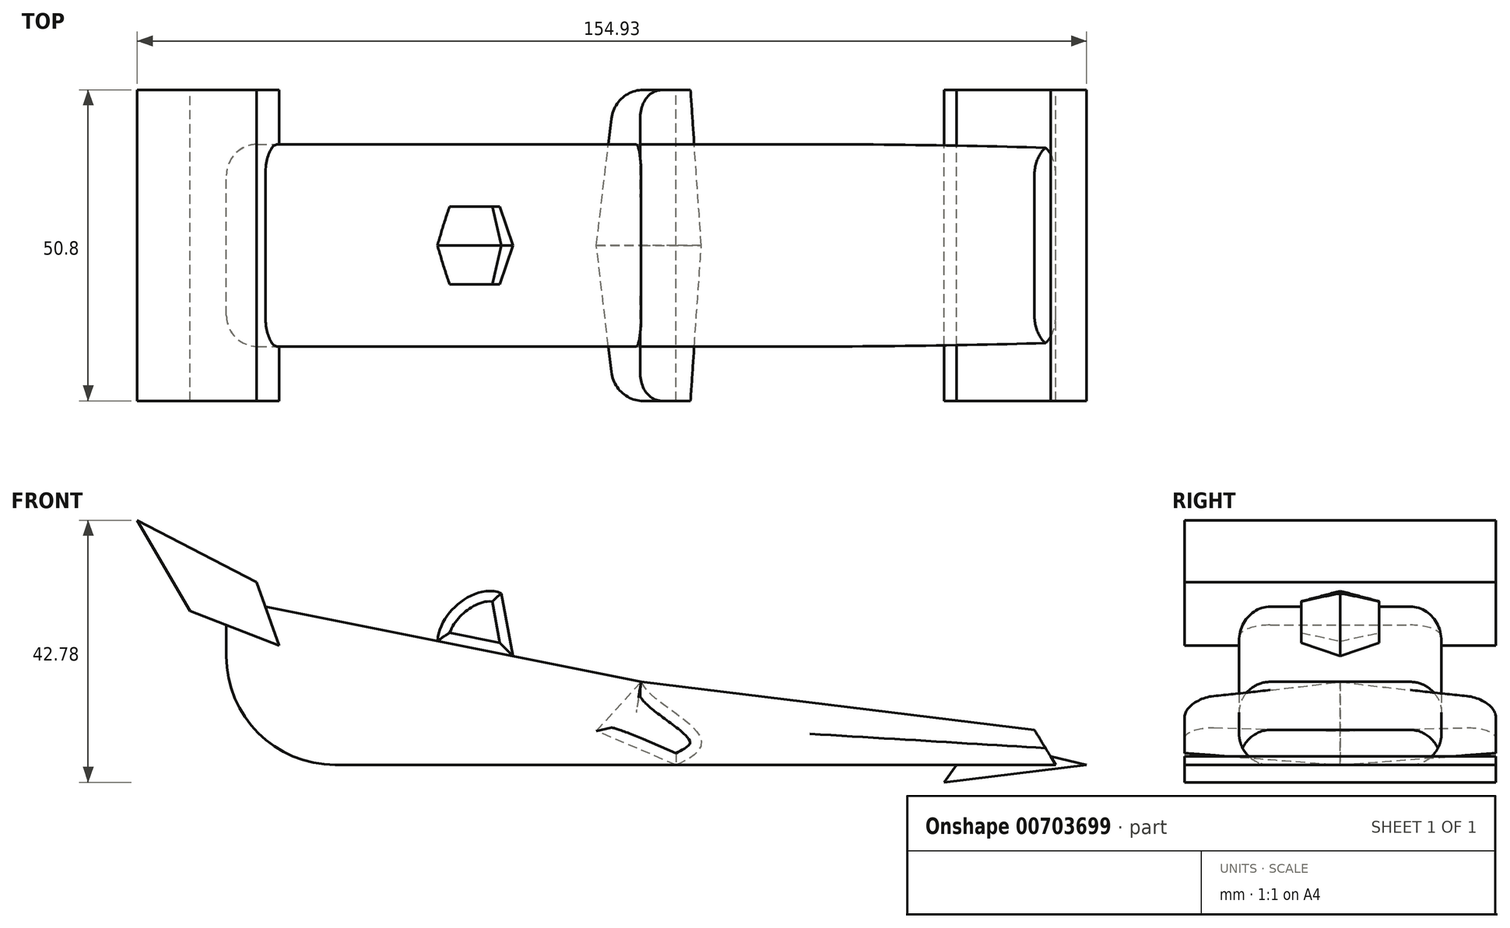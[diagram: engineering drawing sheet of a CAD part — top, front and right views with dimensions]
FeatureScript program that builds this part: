
annotation { "Feature Type Name" : "Feature", "Feature Type Description" : "" }
export const myFeature = defineFeature(function(context is Context, id is Id, definition is map)
    precondition{}
    {
        {
            var Q0;
            Q0=qCreatedBy(makeId("Front.planeOp"),FACE);
            var sketch = newSketch(context, id + "F0", { "sketchPlane" : qUnion([Q0])});
            skLineSegment(sketch, "E0.top", {"start": v(-49.9, -13.56) * mm, "end": v(67.68, -13.56) * mm});
            skLineSegment(sketch, "E0.left", {"start": v(-67.68, 13.56) * mm, "end": v(-67.68, 4.22) * mm});
            skPoint(sketch, "E0.middle", {"position": v(0, 0) * mm});
            skLineSegment(sketch, "E1", {"start": v(-67.68, 13.56) * mm, "end": v(67.68, -13.56) * mm});
            skLineSegment(sketch, "E2", {"start": v(-73.6, 11.59) * mm, "end": v(-59.05, 5.92) * mm});
            skLineSegment(sketch, "E3", {"start": v(-59.05, 5.92) * mm, "end": v(-62.75, 16.27) * mm});
            skLineSegment(sketch, "E4", {"start": v(-62.75, 16.27) * mm, "end": v(-82.23, 26.38) * mm});
            skLineSegment(sketch, "E5", {"start": v(-82.23, 26.38) * mm, "end": v(-73.6, 11.59) * mm});
            skPoint(sketch, "E6.visualSharp", {"position": v(-67.68, -13.56) * mm});
            skArc(sketch, "E6.filletArc", {"start": v(-67.68, 4.22) * mm, "mid": v(-62.47, -8.35) * mm, "end": v(-49.9, -13.56) * mm});
            skLineSegment(sketch, "E7", {"start": v(54.6, -9.2) * mm, "end": v(72.7, -13.56) * mm});
            skLineSegment(sketch, "E8", {"start": v(72.7, -13.56) * mm, "end": v(49.42, -16.4) * mm});
            skLineSegment(sketch, "E9", {"start": v(49.42, -16.4) * mm, "end": v(54.6, -9.2) * mm});
            skLineSegment(sketch, "E10", {"start": v(-20.58, 2.25) * mm, "end": v(-22.8, 14.44) * mm});
            skFitSpline(sketch, "E11", {"points": [v(-22.8, 14.44) * mm, v(-32.22, 3) * mm], "startDerivative": vector(-14.14, 6.72) * mm, "endDerivative": vector(11.97, -18.48) * mm});
            skLineSegment(sketch, "E12", {"start": v(-32.22, 3) * mm, "end": v(-20.58, 2.25) * mm});
            skLineSegment(sketch, "E13", {"start": v(0, 0) * mm, "end": v(64.19, -7.85) * mm});
            skLineSegment(sketch, "E14", {"start": v(64.19, -7.85) * mm, "end": v(67.68, -13.56) * mm});
            skCircle(sketch, "E15", {"center": v(-60.07, -7.54) * mm, "radius": 11.65 * mm});
            skCircle(sketch, "E16", {"center": v(37.55, -8.7) * mm, "radius": 10.46 * mm});
            skFitSpline(sketch, "E17", {"points": [v(0, 0) * mm, v(5.66, -13.56) * mm], "startDerivative": vector(5.66, -13.56) * mm, "endDerivative": vector(-33.9, -13.5) * mm});
            skLineSegment(sketch, "E18", {"start": v(0, 0) * mm, "end": v(-7.3, -8.02) * mm});
            skLineSegment(sketch, "E19", {"start": v(-7.3, -8.02) * mm, "end": v(5.66, -13.56) * mm});
            skSolve(sketch);
        }
        {
            var Q0;
            {var subQ0=sQuery(id+"F0.wireOp",EDGE,"E4");Q0=makeQuery(id+"F0.imprint","IMPRINT",FACE,{"disambiguationData":[TD([[makeQuery(id+"F0.imprint","IMPRINT",EDGE,{"derivedFrom":subQ0}),1.0]])]});}
            var Q1;
            {var subQ0=sQuery(id+"F0.wireOp",EDGE,"E1");var subQ1=sQuery(id+"F0.wireOp",EDGE,"E0.left");var subQ2=makeQuery(id+"F0.imprint","INTERSECT",VERTEX,{"derivedFrom":[subQ1,subQ0]});Q1=makeQuery(id+"F0.imprint","IMPRINT",FACE,{"disambiguationData":[TD([[makeQuery(id+"F0.imprint","IMPRINT",EDGE,{"disambiguationData":[TD([[subQ2,-1.0]])],"derivedFrom":subQ1}),1.0]])]});}
            extrude(context, id + "F1", {"entities" : qUnion([Q0, Q1]), "endBound" : BoundingType.SYMMETRIC, "depth" : 50.8 * mm, "offsetDistance" : 25.4 * mm});
        }
        {
            var Q0;
            {var subQ3=sQuery(id+"F0.wireOp",EDGE,"E16");var subQ8=sQuery(id+"F0.wireOp",EDGE,"E1");var subQ11=makeQuery(id+"F0.imprint","INTERSECT",VERTEX,{"disambiguationData":[OD(1.0)],"derivedFrom":[subQ8,subQ3]});Q0=makeQuery(id+"F0.imprint","IMPRINT",FACE,{"disambiguationData":[TD([[makeQuery(id+"F0.imprint","IMPRINT",EDGE,{"disambiguationData":[TD([[subQ11,-1.0]])],"derivedFrom":subQ8}),1.0]])]});}
            var Q1;
            {var subQ0=sQuery(id+"F0.wireOp",EDGE,"E16");var subQ1=sQuery(id+"F0.wireOp",EDGE,"E0.top");var subQ2=makeQuery(id+"F0.imprint","INTERSECT",VERTEX,{"disambiguationData":[OD(1.0)],"derivedFrom":[subQ1,subQ0]});Q1=makeQuery(id+"F0.imprint","IMPRINT",FACE,{"disambiguationData":[TD([[makeQuery(id+"F0.imprint","IMPRINT",EDGE,{"disambiguationData":[TD([[subQ2,-1.0]])],"derivedFrom":subQ1}),1.0]])]});}
            var Q2;
            {var subQ0=sQuery(id+"F0.wireOp",EDGE,"kRsVcMyl-m4ce-JaHI-SLDY-Nwmdy7v5OAjo");Q2=makeQuery(id+"F0.imprint","IMPRINT",FACE,{"disambiguationData":[TD([[makeQuery(id+"F0.imprint","IMPRINT",EDGE,{"derivedFrom":subQ0}),-1.0]])]});}
            var Q3;
            {var subQ0=sQuery(id+"F0.wireOp",EDGE,"E13");var subQ3=sQuery(id+"F0.wireOp",EDGE,"E16");var subQ5=makeQuery(id+"F0.imprint","INTERSECT",VERTEX,{"disambiguationData":[OD(0.0)],"derivedFrom":[subQ0,subQ3]});Q3=makeQuery(id+"F0.imprint","IMPRINT",FACE,{"disambiguationData":[TD([[makeQuery(id+"F0.imprint","IMPRINT",EDGE,{"disambiguationData":[TD([[subQ5,-1.0]])],"derivedFrom":subQ3}),-1.0]])]});}
            var Q4;
            {var subQ1=sQuery(id+"F0.wireOp",EDGE,"E0.top");var subQ3=sQuery(id+"F0.wireOp",EDGE,"E9");var subQ4=makeQuery(id+"F0.imprint","INTERSECT",VERTEX,{"derivedFrom":[subQ1,subQ3]});Q4=makeQuery(id+"F0.imprint","IMPRINT",FACE,{"disambiguationData":[TD([[makeQuery(id+"F0.imprint","IMPRINT",EDGE,{"disambiguationData":[TD([[subQ4,-1.0]])],"derivedFrom":subQ3}),-1.0]])]});}
            var Q5;
            {var subQ3=sQuery(id+"F0.wireOp",EDGE,"E9");var subQ5=sQuery(id+"F0.wireOp",EDGE,"E7");var subQ6=makeQuery(id+"F0.imprint","INTERSECT",VERTEX,{"derivedFrom":[subQ5,subQ3]});Q5=makeQuery(id+"F0.imprint","IMPRINT",FACE,{"disambiguationData":[TD([[makeQuery(id+"F0.imprint","IMPRINT",EDGE,{"disambiguationData":[TD([[subQ6,-1.0]])],"derivedFrom":subQ5}),-1.0]])]});}
            var Q6;
            {var subQ0=sQuery(id+"F0.wireOp",EDGE,"E16");var subQ1=sQuery(id+"F0.wireOp",EDGE,"E0.top");var subQ2=makeQuery(id+"F0.imprint","INTERSECT",VERTEX,{"disambiguationData":[OD(0.0)],"derivedFrom":[subQ1,subQ0]});Q6=makeQuery(id+"F0.imprint","IMPRINT",FACE,{"disambiguationData":[TD([[makeQuery(id+"F0.imprint","IMPRINT",EDGE,{"disambiguationData":[TD([[subQ2,-1.0]])],"derivedFrom":subQ1}),1.0]])]});}
            var Q7;
            Q7=makeQuery(id+"F0.imprint","IMPRINT",FACE,{"disambiguationData":[TD([[makeQuery(id+"F0.imprint","IMPRINT",EDGE,{"derivedFrom":sQuery(id+"F0.wireOp",EDGE,"868a7912-11ff-420b-9d8f-39dd4aca9dca")}),1.0]])]});
            var Q8;
            {var subQ12=sQuery(id+"F0.wireOp",EDGE,"E12");Q8=makeQuery(id+"F0.imprint","IMPRINT",FACE,{"disambiguationData":[TD([[makeQuery(id+"F0.imprint","IMPRINT",EDGE,{"derivedFrom":subQ12}),-1.0]])]});}
            var Q9;
            {var subQ0=sQuery(id+"F0.wireOp",EDGE,"E15");var subQ1=sQuery(id+"F0.wireOp",EDGE,"E6.filletArc");var subQ2=makeQuery(id+"F0.imprint","INTERSECT",VERTEX,{"disambiguationData":[OD(0.0)],"derivedFrom":[subQ1,subQ0]});Q9=makeQuery(id+"F0.imprint","IMPRINT",FACE,{"disambiguationData":[TD([[makeQuery(id+"F0.imprint","IMPRINT",EDGE,{"disambiguationData":[TD([[subQ2,-1.0]])],"derivedFrom":subQ1}),1.0]])]});}
            var Q10;
            {var subQ5=sQuery(id+"F0.wireOp",EDGE,"E12");Q10=makeQuery(id+"F0.imprint","IMPRINT",FACE,{"disambiguationData":[TD([[makeQuery(id+"F0.imprint","IMPRINT",EDGE,{"derivedFrom":subQ5}),1.0]])]});}
            var Q11;
            {var subQ0=sQuery(id+"F0.wireOp",EDGE,"E16");var subQ1=sQuery(id+"F0.wireOp",EDGE,"E1");var subQ2=makeQuery(id+"F0.imprint","INTERSECT",VERTEX,{"disambiguationData":[OD(0.0)],"derivedFrom":[subQ1,subQ0]});Q11=makeQuery(id+"F0.imprint","IMPRINT",FACE,{"disambiguationData":[TD([[makeQuery(id+"F0.imprint","IMPRINT",EDGE,{"disambiguationData":[TD([[subQ2,-1.0]])],"derivedFrom":subQ1}),1.0]])]});}
            var Q12;
            {var subQ0=sQuery(id+"F0.wireOp",EDGE,"E17");Q12=makeQuery(id+"F0.imprint","IMPRINT",FACE,{"disambiguationData":[TD([[makeQuery(id+"F0.imprint","IMPRINT",EDGE,{"derivedFrom":subQ0}),1.0]])]});}
            var Q13;
            Q13=makeQuery(id+"F0.imprint","IMPRINT",FACE,{"disambiguationData":[TD([[makeQuery(id+"F0.imprint","IMPRINT",EDGE,{"derivedFrom":sQuery(id+"F0.wireOp",EDGE,"E17")}),-1.0]])]});
            extrude(context, id + "F2", {"entities" : qUnion([Q0, Q1, Q2, Q3, Q4, Q5, Q6, Q7, Q8, Q9, Q10, Q11, Q12, Q13]), "operationType" : NewBodyOperationType.ADD, "endBound" : BoundingType.SYMMETRIC, "depth" : 33.02 * mm, "offsetDistance" : 25.4 * mm});
        }
        {
            var Q0;
            Q0=makeQuery(id+"F2.opExtrude","CAP_EDGE",EDGE,{"disambiguationData":[OSD([sQuery(id+"F0.wireOp",EDGE,"E1")])],"isStart":false});
            var Q1;
            Q1=makeQuery(id+"F2.opExtrude","CAP_EDGE",EDGE,{"disambiguationData":[OSD([sQuery(id+"F0.wireOp",EDGE,"E1")])],"isStart":true});
            var Q2;
            Q2=makeQuery(id+"F2.opExtrude","CAP_EDGE",EDGE,{"disambiguationData":[OSD([sQuery(id+"F0.wireOp",EDGE,"E0.top")])],"isStart":false});
            var Q3;
            Q3=makeQuery(id+"F2.opExtrude","CAP_EDGE",EDGE,{"disambiguationData":[OSD([sQuery(id+"F0.wireOp",EDGE,"E0.top")])],"isStart":true});
            fillet(context, id + "F3", {"entities" : qUnion([Q0, Q1, Q2, Q3]), "radius" : 5.08 * mm, "tangentPropagation" : true, "allowEdgeOverflow" : false});
        }
        {
            var Q0;
            Q0=makeQuery(id+"F0.imprint","IMPRINT",FACE,{"disambiguationData":[TD([[makeQuery(id+"F0.imprint","IMPRINT",EDGE,{"derivedFrom":sQuery(id+"F0.wireOp",EDGE,"E17")}),-1.0]])]});
            extrude(context, id + "F4", {"entities" : qUnion([Q0]), "endBound" : BoundingType.SYMMETRIC, "depth" : 50.8 * mm, "offsetDistance" : 25.4 * mm, "hasDraft" : true, "draftAngle" : 4 * degree, "draftPullDirection" : true});
        }
        {
            var Q0;
            Q0=makeQuery(id+"F4.opExtrude","CAP_EDGE",EDGE,{"disambiguationData":[OSD([sQuery(id+"F0.wireOp",EDGE,"E18")])],"isStart":false});
            var Q1;
            Q1=makeQuery(id+"F4.opExtrude","CAP_EDGE",EDGE,{"disambiguationData":[OSD([sQuery(id+"F0.wireOp",EDGE,"E18")])],"isStart":true});
            fillet(context, id + "F5", {"entities" : qUnion([Q0, Q1]), "radius" : 5.08 * mm, "tangentPropagation" : true, "allowEdgeOverflow" : false});
        }
        {
            var Q0;
            {var subQ1=sQuery(id+"F0.wireOp",EDGE,"E8");Q0=makeQuery(id+"F0.imprint","IMPRINT",FACE,{"disambiguationData":[TD([[makeQuery(id+"F0.imprint","IMPRINT",EDGE,{"derivedFrom":subQ1}),-1.0]])]});}
            extrude(context, id + "F6", {"entities" : qUnion([Q0]), "endBound" : BoundingType.SYMMETRIC, "depth" : 50.8 * mm, "offsetDistance" : 25.4 * mm});
        }
        {
            var Q0;
            {var subQ0=sQuery(id+"F0.wireOp",EDGE,"E11");var subQ1=sQuery(id+"F0.wireOp",EDGE,"E1");var subQ2=makeQuery(id+"F0.imprint","INTERSECT",VERTEX,{"derivedFrom":[subQ1,subQ0]});Q0=makeQuery(id+"F0.imprint","IMPRINT",FACE,{"disambiguationData":[TD([[makeQuery(id+"F0.imprint","IMPRINT",EDGE,{"disambiguationData":[TD([[subQ2,-1.0]])],"derivedFrom":subQ1}),1.0]])]});}
            extrude(context, id + "F7", {"entities" : qUnion([Q0]), "endBound" : BoundingType.SYMMETRIC, "depth" : 12.7 * mm, "offsetDistance" : 25.4 * mm, "hasDraft" : true, "draftAngle" : 15 * degree, "draftPullDirection" : true});
        }
    });
